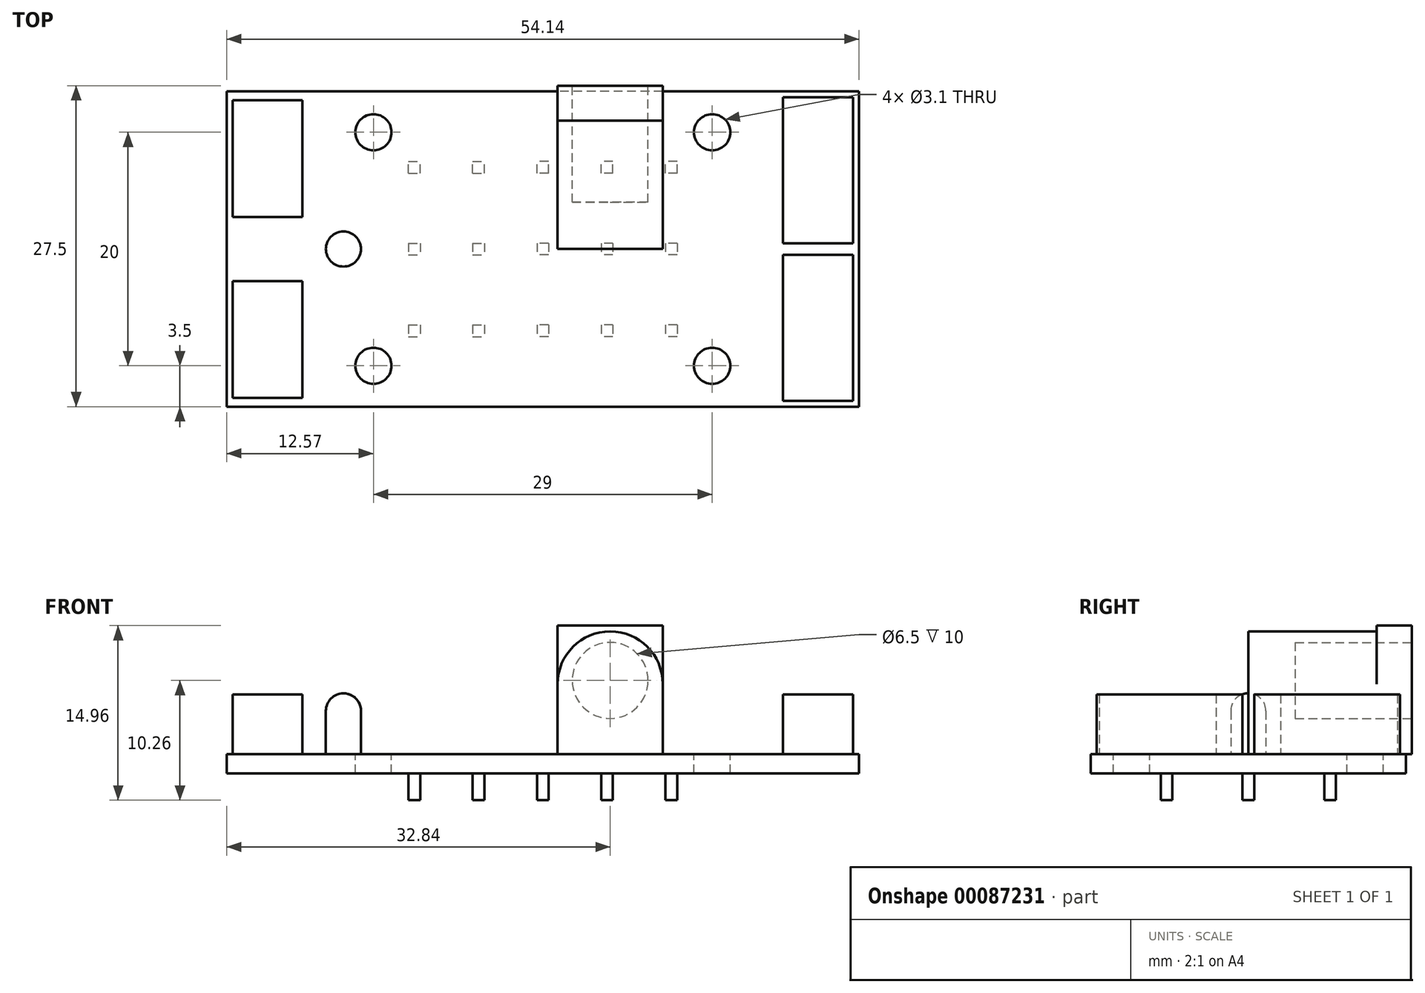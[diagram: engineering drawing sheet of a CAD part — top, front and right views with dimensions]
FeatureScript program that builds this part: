
annotation { "Feature Type Name" : "Feature", "Feature Type Description" : "" }
export const myFeature = defineFeature(function(context is Context, id is Id, definition is map)
    precondition{}
    {
        {
            var Q0;
            Q0=qCreatedBy(makeId("Top.planeOp"),FACE);
            var sketch = newSketch(context, id + "F0", { "sketchPlane" : qUnion([Q0])});
            skLineSegment(sketch, "E0.bottom", {"start": v(27.07, -13.5) * mm, "end": v(-27.07, -13.5) * mm});
            skLineSegment(sketch, "E0.top", {"start": v(27.07, 13.5) * mm, "end": v(-27.07, 13.5) * mm});
            skLineSegment(sketch, "E0.left", {"start": v(27.07, -13.5) * mm, "end": v(27.07, 13.5) * mm});
            skLineSegment(sketch, "E0.right", {"start": v(-27.07, -13.5) * mm, "end": v(-27.07, 13.5) * mm});
            skPoint(sketch, "E0.middle", {"position": v(0, 0) * mm});
            skCircle(sketch, "E1", {"center": v(-14.5, 10) * mm, "radius": 1.55 * mm});
            skCircle(sketch, "E2.MirrorC", {"center": v(14.5, 10) * mm, "radius": 1.55 * mm});
            skCircle(sketch, "E3.MirrorC", {"center": v(14.5, -10) * mm, "radius": 1.55 * mm});
            skCircle(sketch, "E4.MirrorC", {"center": v(-14.5, -10) * mm, "radius": 1.55 * mm});
            skLineSegment(sketch, "E5.bottom", {"start": v(26.57, 0.5) * mm, "end": v(20.57, 0.5) * mm});
            skLineSegment(sketch, "E5.top", {"start": v(26.57, 13) * mm, "end": v(20.57, 13) * mm});
            skLineSegment(sketch, "E5.left", {"start": v(26.57, 0.5) * mm, "end": v(26.57, 13) * mm});
            skLineSegment(sketch, "E5.right", {"start": v(20.57, 0.5) * mm, "end": v(20.57, 13) * mm});
            skPoint(sketch, "E5.middle", {"position": v(23.57, 6.75) * mm});
            skLineSegment(sketch, "E6.MirrorCS", {"start": v(26.57, -0.5) * mm, "end": v(20.57, -0.5) * mm});
            skLineSegment(sketch, "E7.MirrorCS", {"start": v(26.57, -0.5) * mm, "end": v(26.57, -13) * mm});
            skLineSegment(sketch, "E8.MirrorCS", {"start": v(20.57, -0.5) * mm, "end": v(20.57, -13) * mm});
            skLineSegment(sketch, "E9.MirrorCS", {"start": v(26.57, -13) * mm, "end": v(20.57, -13) * mm});
            skLineSegment(sketch, "E10.bottom", {"start": v(10.27, 0) * mm, "end": v(1.27, 0) * mm});
            skLineSegment(sketch, "E10.top", {"start": v(10.27, 14) * mm, "end": v(1.27, 14) * mm});
            skLineSegment(sketch, "E10.left", {"start": v(10.27, 0) * mm, "end": v(10.27, 14) * mm});
            skLineSegment(sketch, "E10.right", {"start": v(1.27, 0) * mm, "end": v(1.27, 14) * mm});
            skPoint(sketch, "E10.middle", {"position": v(5.77, 7) * mm});
            skLineSegment(sketch, "E11.bottom", {"start": v(-11.07, -11) * mm, "end": v(-1.07, -11) * mm});
            skLineSegment(sketch, "E11.top", {"start": v(-11.07, 11) * mm, "end": v(-1.07, 11) * mm});
            skLineSegment(sketch, "E11.left", {"start": v(-11.07, -11) * mm, "end": v(-11.07, 11) * mm});
            skLineSegment(sketch, "E11.right", {"start": v(-1.07, -11) * mm, "end": v(-1.07, 11) * mm});
            skPoint(sketch, "E11.middle", {"position": v(-6.07, 0) * mm});
            skCircle(sketch, "E12", {"center": v(-17.07, 0) * mm, "radius": 1.5 * mm});
            skLineSegment(sketch, "E13.bottom", {"start": v(-20.57, 2.75) * mm, "end": v(-26.57, 2.75) * mm});
            skLineSegment(sketch, "E13.top", {"start": v(-20.57, 12.75) * mm, "end": v(-26.57, 12.75) * mm});
            skLineSegment(sketch, "E13.left", {"start": v(-20.57, 2.75) * mm, "end": v(-20.57, 12.75) * mm});
            skLineSegment(sketch, "E13.right", {"start": v(-26.57, 2.75) * mm, "end": v(-26.57, 12.75) * mm});
            skPoint(sketch, "E13.middle", {"position": v(-23.57, 7.75) * mm});
            skLineSegment(sketch, "E14.MirrorCS", {"start": v(-20.57, -2.75) * mm, "end": v(-26.57, -2.75) * mm});
            skLineSegment(sketch, "E15.MirrorCS", {"start": v(-26.57, -2.75) * mm, "end": v(-26.57, -12.75) * mm});
            skLineSegment(sketch, "E16.MirrorCS", {"start": v(-20.57, -2.75) * mm, "end": v(-20.57, -12.75) * mm});
            skLineSegment(sketch, "E17.MirrorCS", {"start": v(-20.57, -12.75) * mm, "end": v(-26.57, -12.75) * mm});
            skLineSegment(sketch, "E18", {"start": v(1.27, 11) * mm, "end": v(10.27, 11) * mm});
            skSolve(sketch);
        }
        {
            var Q0;
            Q0=makeQuery(id+"F0.imprint","IMPRINT",FACE,{"disambiguationData":[TD([[makeQuery(id+"F0.imprint","IMPRINT",EDGE,{"derivedFrom":sQuery(id+"F0.wireOp",EDGE,"E13.bottom")}),-1.0]])]});
            var Q1;
            Q1=makeQuery(id+"F0.imprint","IMPRINT",FACE,{"disambiguationData":[TD([[makeQuery(id+"F0.imprint","IMPRINT",EDGE,{"derivedFrom":sQuery(id+"F0.wireOp",EDGE,"E0.bottom")}),-1.0]])]});
            var Q2;
            Q2=makeQuery(id+"F0.imprint","IMPRINT",FACE,{"disambiguationData":[TD([[makeQuery(id+"F0.imprint","IMPRINT",EDGE,{"derivedFrom":sQuery(id+"F0.wireOp",EDGE,"E14.MirrorCS")}),1.0]])]});
            var Q3;
            Q3=makeQuery(id+"F0.imprint","IMPRINT",FACE,{"disambiguationData":[TD([[makeQuery(id+"F0.imprint","IMPRINT",EDGE,{"derivedFrom":sQuery(id+"F0.wireOp",EDGE,"E11.bottom")}),1.0]])]});
            var Q4;
            {var subQ5=sQuery(id+"F0.wireOp",EDGE,"E10.bottom");Q4=makeQuery(id+"F0.imprint","IMPRINT",FACE,{"disambiguationData":[TD([[makeQuery(id+"F0.imprint","IMPRINT",EDGE,{"derivedFrom":subQ5}),-1.0]])]});}
            var Q5;
            Q5=makeQuery(id+"F0.imprint","IMPRINT",FACE,{"disambiguationData":[TD([[makeQuery(id+"F0.imprint","IMPRINT",EDGE,{"derivedFrom":sQuery(id+"F0.wireOp",EDGE,"E5.bottom")}),-1.0]])]});
            var Q6;
            Q6=makeQuery(id+"F0.imprint","IMPRINT",FACE,{"disambiguationData":[TD([[makeQuery(id+"F0.imprint","IMPRINT",EDGE,{"derivedFrom":sQuery(id+"F0.wireOp",EDGE,"E6.MirrorCS")}),1.0]])]});
            var Q7;
            Q7=makeQuery(id+"F0.imprint","IMPRINT",FACE,{"disambiguationData":[TD([[makeQuery(id+"F0.imprint","IMPRINT",EDGE,{"derivedFrom":sQuery(id+"F0.wireOp",EDGE,"E12")}),1.0]])]});
            var Q8;
            {var subQ5=sQuery(id+"F0.wireOp",EDGE,"E18");Q8=makeQuery(id+"F0.imprint","IMPRINT",FACE,{"disambiguationData":[TD([[makeQuery(id+"F0.imprint","IMPRINT",EDGE,{"derivedFrom":subQ5}),1.0]])]});}
            extrude(context, id + "F1", {"entities" : qUnion([Q0, Q1, Q2, Q3, Q4, Q5, Q6, Q7, Q8]), "oppositeDirection" : true, "depth" : 1.66 * mm});
        }
        {
            var Q0;
            {var subQ5=sQuery(id+"F0.wireOp",EDGE,"E18");Q0=makeQuery(id+"F0.imprint","IMPRINT",FACE,{"disambiguationData":[TD([[makeQuery(id+"F0.imprint","IMPRINT",EDGE,{"derivedFrom":subQ5}),1.0]])]});}
            var Q1;
            {var subQ5=sQuery(id+"F0.wireOp",EDGE,"E10.top");Q1=makeQuery(id+"F0.imprint","IMPRINT",FACE,{"disambiguationData":[TD([[makeQuery(id+"F0.imprint","IMPRINT",EDGE,{"derivedFrom":subQ5}),1.0]])]});}
            extrude(context, id + "F2", {"entities" : qUnion([Q0, Q1]), "depth" : 11 * mm});
        }
        {
            var Q0;
            {var subQ0=sQuery(id+"F0.wireOp",EDGE,"E10.bottom");Q0=makeQuery(id+"F0.imprint","IMPRINT",FACE,{"disambiguationData":[TD([[makeQuery(id+"F0.imprint","IMPRINT",EDGE,{"derivedFrom":subQ0}),-1.0]])]});}
            extrude(context, id + "F3", {"entities" : qUnion([Q0]), "operationType" : NewBodyOperationType.ADD, "depth" : 10.5 * mm});
        }
        {
            var Q0;
            Q0=makeQuery(id+"F3.opExtrude","CAP_EDGE",EDGE,{"disambiguationData":[OSD([sQuery(id+"F0.wireOp",EDGE,"E10.right")])],"isStart":false});
            var Q1;
            Q1=makeQuery(id+"F3.opExtrude","CAP_EDGE",EDGE,{"disambiguationData":[OSD([sQuery(id+"F0.wireOp",EDGE,"E10.left")])],"isStart":false});
            fillet(context, id + "F4", {"entities" : qUnion([Q0, Q1]), "radius" : 4.5 * mm, "tangentPropagation" : true, "allowEdgeOverflow" : false});
        }
        {
            var Q0;
            Q0=makeQuery(id+"F2.opExtrude","SWEPT_FACE",FACE,{"disambiguationData":[OSD([sQuery(id+"F0.wireOp",EDGE,"E10.top")])]});
            var sketch = newSketch(context, id + "F5", { "sketchPlane" : qUnion([Q0])});
            skCircle(sketch, "E19", {"center": v(-5.77, 6.3) * mm, "radius": 3.25 * mm});
            skPoint(sketch, "E19.centerSnap0", {"position": v(-5.77, 0) * mm});
            skSolve(sketch);
        }
        {
            var Q0;
            Q0=makeQuery(id+"F5.imprint","IMPRINT",FACE,{"disambiguationData":[TD([[makeQuery(id+"F5.imprint","IMPRINT",EDGE,{"derivedFrom":sQuery(id+"F5.wireOp",EDGE,"E19")}),1.0]])]});
            extrude(context, id + "F6", {"entities" : qUnion([Q0]), "operationType" : NewBodyOperationType.REMOVE, "oppositeDirection" : true, "depth" : 10 * mm});
        }
        {
            var Q0;
            Q0=makeQuery(id+"F0.imprint","IMPRINT",FACE,{"disambiguationData":[TD([[makeQuery(id+"F0.imprint","IMPRINT",EDGE,{"derivedFrom":sQuery(id+"F0.wireOp",EDGE,"E12")}),1.0]])]});
            extrude(context, id + "F7", {"entities" : qUnion([Q0]), "depth" : 5.2 * mm});
        }
        {
            var Q0;
            Q0=makeQuery(id+"F7.opExtrude","CAP_EDGE",EDGE,{"disambiguationData":[OSD([sQuery(id+"F0.wireOp",EDGE,"E12")])],"isStart":false});
            fillet(context, id + "F8", {"entities" : qUnion([Q0]), "radius" : 1.5 * mm, "tangentPropagation" : true, "allowEdgeOverflow" : false});
        }
        {
            var Q0;
            Q0=makeQuery(id+"F0.imprint","IMPRINT",FACE,{"disambiguationData":[TD([[makeQuery(id+"F0.imprint","IMPRINT",EDGE,{"derivedFrom":sQuery(id+"F0.wireOp",EDGE,"E5.bottom")}),-1.0]])]});
            var Q1;
            Q1=makeQuery(id+"F0.imprint","IMPRINT",FACE,{"disambiguationData":[TD([[makeQuery(id+"F0.imprint","IMPRINT",EDGE,{"derivedFrom":sQuery(id+"F0.wireOp",EDGE,"E6.MirrorCS")}),1.0]])]});
            var Q2;
            Q2=makeQuery(id+"F0.imprint","IMPRINT",FACE,{"disambiguationData":[TD([[makeQuery(id+"F0.imprint","IMPRINT",EDGE,{"derivedFrom":sQuery(id+"F0.wireOp",EDGE,"E14.MirrorCS")}),1.0]])]});
            var Q3;
            Q3=makeQuery(id+"F0.imprint","IMPRINT",FACE,{"disambiguationData":[TD([[makeQuery(id+"F0.imprint","IMPRINT",EDGE,{"derivedFrom":sQuery(id+"F0.wireOp",EDGE,"E13.bottom")}),-1.0]])]});
            extrude(context, id + "F9", {"entities" : qUnion([Q0, Q1, Q2, Q3]), "depth" : 5.1 * mm});
        }
        {
            var Q0;
            Q0=makeQuery(id+"F1.opExtrude","CAP_FACE",FACE,{"disambiguationData":[OSD([sQuery(id+"F0.wireOp",EDGE,"E0.bottom"),sQuery(id+"F0.wireOp",EDGE,"E0.top"),sQuery(id+"F0.wireOp",EDGE,"E0.left"),sQuery(id+"F0.wireOp",EDGE,"E0.right"),sQuery(id+"F0.wireOp",EDGE,"E1"),sQuery(id+"F0.wireOp",EDGE,"E2.MirrorC"),sQuery(id+"F0.wireOp",EDGE,"E3.MirrorC"),sQuery(id+"F0.wireOp",EDGE,"E4.MirrorC")])],"isStart":false});
            var sketch = newSketch(context, id + "F10", { "sketchPlane" : qUnion([Q0])});
            skLineSegment(sketch, "E20.bottom", {"start": v(0.5, -0.5) * mm, "end": v(-0.5, -0.5) * mm});
            skLineSegment(sketch, "E20.top", {"start": v(0.5, 0.5) * mm, "end": v(-0.5, 0.5) * mm});
            skLineSegment(sketch, "E20.left", {"start": v(0.5, -0.5) * mm, "end": v(0.5, 0.5) * mm});
            skLineSegment(sketch, "E20.right", {"start": v(-0.5, -0.5) * mm, "end": v(-0.5, 0.5) * mm});
            skPoint(sketch, "E20.middle", {"position": v(0, 0) * mm});
            skLineSegment(sketch, "E21.0.1.0", {"start": v(0.5, 6.5) * mm, "end": v(0.5, 7.5) * mm});
            skLineSegment(sketch, "E21.0.1.1", {"start": v(0.5, 7.5) * mm, "end": v(-0.5, 7.5) * mm});
            skLineSegment(sketch, "E21.0.1.2", {"start": v(-0.5, 6.5) * mm, "end": v(-0.5, 7.5) * mm});
            skLineSegment(sketch, "E21.0.1.3", {"start": v(0.5, 6.5) * mm, "end": v(-0.5, 6.5) * mm});
            skLineSegment(sketch, "E21.1.0.0", {"start": v(6, -0.5) * mm, "end": v(6, 0.5) * mm});
            skLineSegment(sketch, "E21.1.0.1", {"start": v(6, 0.5) * mm, "end": v(5, 0.5) * mm});
            skLineSegment(sketch, "E21.1.0.2", {"start": v(5, -0.5) * mm, "end": v(5, 0.5) * mm});
            skLineSegment(sketch, "E21.1.0.3", {"start": v(6, -0.5) * mm, "end": v(5, -0.5) * mm});
            skLineSegment(sketch, "E21.1.1.0", {"start": v(6, 6.5) * mm, "end": v(6, 7.5) * mm});
            skLineSegment(sketch, "E21.1.1.1", {"start": v(6, 7.5) * mm, "end": v(5, 7.5) * mm});
            skLineSegment(sketch, "E21.1.1.2", {"start": v(5, 6.5) * mm, "end": v(5, 7.5) * mm});
            skLineSegment(sketch, "E21.1.1.3", {"start": v(6, 6.5) * mm, "end": v(5, 6.5) * mm});
            skLineSegment(sketch, "E21.2.0.0", {"start": v(11.5, -0.5) * mm, "end": v(11.5, 0.5) * mm});
            skLineSegment(sketch, "E21.2.0.1", {"start": v(11.5, 0.5) * mm, "end": v(10.5, 0.5) * mm});
            skLineSegment(sketch, "E21.2.0.2", {"start": v(10.5, -0.5) * mm, "end": v(10.5, 0.5) * mm});
            skLineSegment(sketch, "E21.2.0.3", {"start": v(11.5, -0.5) * mm, "end": v(10.5, -0.5) * mm});
            skLineSegment(sketch, "E21.2.1.0", {"start": v(11.5, 6.5) * mm, "end": v(11.5, 7.5) * mm});
            skLineSegment(sketch, "E21.2.1.1", {"start": v(11.5, 7.5) * mm, "end": v(10.5, 7.5) * mm});
            skLineSegment(sketch, "E21.2.1.2", {"start": v(10.5, 6.5) * mm, "end": v(10.5, 7.5) * mm});
            skLineSegment(sketch, "E21.2.1.3", {"start": v(11.5, 6.5) * mm, "end": v(10.5, 6.5) * mm});
            skLineSegment(sketch, "E21.direction1", {"start": v(0.5, -0.5) * mm, "end": v(6, -0.5) * mm, "construction": true});
            skLineSegment(sketch, "E21.direction2", {"start": v(0.5, -0.5) * mm, "end": v(0.5, 6.5) * mm, "construction": true});
            skLineSegment(sketch, "E22.MirrorCS", {"start": v(11.5, -6.5) * mm, "end": v(10.5, -6.5) * mm});
            skLineSegment(sketch, "E23.MirrorCS", {"start": v(11.5, -6.5) * mm, "end": v(11.5, -7.5) * mm});
            skLineSegment(sketch, "E24.MirrorCS", {"start": v(11.5, -7.5) * mm, "end": v(10.5, -7.5) * mm});
            skLineSegment(sketch, "E25.MirrorCS", {"start": v(10.5, -6.5) * mm, "end": v(10.5, -7.5) * mm});
            skLineSegment(sketch, "E26.MirrorCS", {"start": v(6, -6.5) * mm, "end": v(5, -6.5) * mm});
            skLineSegment(sketch, "E27.MirrorCS", {"start": v(6, -6.5) * mm, "end": v(6, -7.5) * mm});
            skLineSegment(sketch, "E28.MirrorCS", {"start": v(6, -7.5) * mm, "end": v(5, -7.5) * mm});
            skLineSegment(sketch, "E29.MirrorCS", {"start": v(5, -6.5) * mm, "end": v(5, -7.5) * mm});
            skLineSegment(sketch, "E30.MirrorCS", {"start": v(0.5, -6.5) * mm, "end": v(-0.5, -6.5) * mm});
            skLineSegment(sketch, "E31.MirrorCS", {"start": v(-0.5, -6.5) * mm, "end": v(-0.5, -7.5) * mm});
            skLineSegment(sketch, "E32.MirrorCS", {"start": v(0.5, -6.5) * mm, "end": v(0.5, -7.5) * mm});
            skLineSegment(sketch, "E33.MirrorCS", {"start": v(0.5, -7.5) * mm, "end": v(-0.5, -7.5) * mm});
            skLineSegment(sketch, "E34.MirrorCS", {"start": v(-6, -6.5) * mm, "end": v(-6, -7.5) * mm});
            skLineSegment(sketch, "E35.MirrorCS", {"start": v(-10.5, 6.5) * mm, "end": v(-10.5, 7.5) * mm});
            skLineSegment(sketch, "E36.MirrorCS", {"start": v(-11.5, -0.5) * mm, "end": v(-10.5, -0.5) * mm});
            skLineSegment(sketch, "E37.MirrorCS", {"start": v(-11.5, -6.5) * mm, "end": v(-10.5, -6.5) * mm});
            skLineSegment(sketch, "E38.MirrorCS", {"start": v(-10.5, -0.5) * mm, "end": v(-10.5, 0.5) * mm});
            skLineSegment(sketch, "E39.MirrorCS", {"start": v(-0.5, -0.5) * mm, "end": v(-6, -0.5) * mm, "construction": true});
            skLineSegment(sketch, "E40.MirrorCS", {"start": v(-11.5, 7.5) * mm, "end": v(-10.5, 7.5) * mm});
            skLineSegment(sketch, "E41.MirrorCS", {"start": v(-6, -6.5) * mm, "end": v(-5, -6.5) * mm});
            skLineSegment(sketch, "E42.MirrorCS", {"start": v(-11.5, -6.5) * mm, "end": v(-11.5, -7.5) * mm});
            skLineSegment(sketch, "E43.MirrorCS", {"start": v(-11.5, -0.5) * mm, "end": v(-11.5, 0.5) * mm});
            skLineSegment(sketch, "E44.MirrorCS", {"start": v(-6, -7.5) * mm, "end": v(-5, -7.5) * mm});
            skLineSegment(sketch, "E45.MirrorCS", {"start": v(-5, 6.5) * mm, "end": v(-5, 7.5) * mm});
            skLineSegment(sketch, "E46.MirrorCS", {"start": v(-6, 6.5) * mm, "end": v(-5, 6.5) * mm});
            skLineSegment(sketch, "E47.MirrorCS", {"start": v(-11.5, -7.5) * mm, "end": v(-10.5, -7.5) * mm});
            skLineSegment(sketch, "E48.MirrorCS", {"start": v(-11.5, 0.5) * mm, "end": v(-10.5, 0.5) * mm});
            skLineSegment(sketch, "E49.MirrorCS", {"start": v(-5, -6.5) * mm, "end": v(-5, -7.5) * mm});
            skLineSegment(sketch, "E50.MirrorCS", {"start": v(-11.5, 6.5) * mm, "end": v(-10.5, 6.5) * mm});
            skLineSegment(sketch, "E51.MirrorCS", {"start": v(-6, 7.5) * mm, "end": v(-5, 7.5) * mm});
            skLineSegment(sketch, "E52.MirrorCS", {"start": v(-6, 6.5) * mm, "end": v(-6, 7.5) * mm});
            skLineSegment(sketch, "E53.MirrorCS", {"start": v(-6, -0.5) * mm, "end": v(-5, -0.5) * mm});
            skLineSegment(sketch, "E54.MirrorCS", {"start": v(-5, -0.5) * mm, "end": v(-5, 0.5) * mm});
            skLineSegment(sketch, "E55.MirrorCS", {"start": v(-11.5, 6.5) * mm, "end": v(-11.5, 7.5) * mm});
            skLineSegment(sketch, "E56.MirrorCS", {"start": v(-6, 0.5) * mm, "end": v(-5, 0.5) * mm});
            skLineSegment(sketch, "E57.MirrorCS", {"start": v(-10.5, -6.5) * mm, "end": v(-10.5, -7.5) * mm});
            skLineSegment(sketch, "E58.MirrorCS", {"start": v(-6, -0.5) * mm, "end": v(-6, 0.5) * mm});
            skSolve(sketch);
        }
        {
            var Q0;
            Q0=makeQuery(id+"F10.imprint","IMPRINT",FACE,{"disambiguationData":[TD([[makeQuery(id+"F10.imprint","IMPRINT",EDGE,{"derivedFrom":sQuery(id+"F10.wireOp",EDGE,"E20.bottom")}),-1.0]])]});
            var Q1;
            Q1=makeQuery(id+"F10.imprint","IMPRINT",FACE,{"disambiguationData":[TD([[makeQuery(id+"F10.imprint","IMPRINT",EDGE,{"derivedFrom":sQuery(id+"F10.wireOp",EDGE,"E21.0.1.0")}),1.0]])]});
            var Q2;
            Q2=makeQuery(id+"F10.imprint","IMPRINT",FACE,{"disambiguationData":[TD([[makeQuery(id+"F10.imprint","IMPRINT",EDGE,{"derivedFrom":sQuery(id+"F10.wireOp",EDGE,"E21.1.1.0")}),1.0]])]});
            var Q3;
            Q3=makeQuery(id+"F10.imprint","IMPRINT",FACE,{"disambiguationData":[TD([[makeQuery(id+"F10.imprint","IMPRINT",EDGE,{"derivedFrom":sQuery(id+"F10.wireOp",EDGE,"E21.2.1.0")}),1.0]])]});
            var Q4;
            Q4=makeQuery(id+"F10.imprint","IMPRINT",FACE,{"disambiguationData":[TD([[makeQuery(id+"F10.imprint","IMPRINT",EDGE,{"derivedFrom":sQuery(id+"F10.wireOp",EDGE,"E21.2.0.0")}),1.0]])]});
            var Q5;
            Q5=makeQuery(id+"F10.imprint","IMPRINT",FACE,{"disambiguationData":[TD([[makeQuery(id+"F10.imprint","IMPRINT",EDGE,{"derivedFrom":sQuery(id+"F10.wireOp",EDGE,"E21.1.0.0")}),1.0]])]});
            var Q6;
            Q6=makeQuery(id+"F10.imprint","IMPRINT",FACE,{"disambiguationData":[TD([[makeQuery(id+"F10.imprint","IMPRINT",EDGE,{"derivedFrom":sQuery(id+"F10.wireOp",EDGE,"E22.MirrorCS")}),1.0]])]});
            var Q7;
            Q7=makeQuery(id+"F10.imprint","IMPRINT",FACE,{"disambiguationData":[TD([[makeQuery(id+"F10.imprint","IMPRINT",EDGE,{"derivedFrom":sQuery(id+"F10.wireOp",EDGE,"E26.MirrorCS")}),1.0]])]});
            var Q8;
            Q8=makeQuery(id+"F10.imprint","IMPRINT",FACE,{"disambiguationData":[TD([[makeQuery(id+"F10.imprint","IMPRINT",EDGE,{"derivedFrom":sQuery(id+"F10.wireOp",EDGE,"E30.MirrorCS")}),1.0]])]});
            var Q9;
            Q9=makeQuery(id+"F10.imprint","IMPRINT",FACE,{"disambiguationData":[TD([[makeQuery(id+"F10.imprint","IMPRINT",EDGE,{"derivedFrom":sQuery(id+"F10.wireOp",EDGE,"E34.MirrorCS")}),1.0]])]});
            var Q10;
            Q10=makeQuery(id+"F10.imprint","IMPRINT",FACE,{"disambiguationData":[TD([[makeQuery(id+"F10.imprint","IMPRINT",EDGE,{"derivedFrom":sQuery(id+"F10.wireOp",EDGE,"E53.MirrorCS")}),1.0]])]});
            var Q11;
            Q11=makeQuery(id+"F10.imprint","IMPRINT",FACE,{"disambiguationData":[TD([[makeQuery(id+"F10.imprint","IMPRINT",EDGE,{"derivedFrom":sQuery(id+"F10.wireOp",EDGE,"E46.MirrorCS")}),1.0]])]});
            var Q12;
            Q12=makeQuery(id+"F10.imprint","IMPRINT",FACE,{"disambiguationData":[TD([[makeQuery(id+"F10.imprint","IMPRINT",EDGE,{"derivedFrom":sQuery(id+"F10.wireOp",EDGE,"E35.MirrorCS")}),1.0]])]});
            var Q13;
            Q13=makeQuery(id+"F10.imprint","IMPRINT",FACE,{"disambiguationData":[TD([[makeQuery(id+"F10.imprint","IMPRINT",EDGE,{"derivedFrom":sQuery(id+"F10.wireOp",EDGE,"E36.MirrorCS")}),1.0]])]});
            var Q14;
            Q14=makeQuery(id+"F10.imprint","IMPRINT",FACE,{"disambiguationData":[TD([[makeQuery(id+"F10.imprint","IMPRINT",EDGE,{"derivedFrom":sQuery(id+"F10.wireOp",EDGE,"E37.MirrorCS")}),-1.0]])]});
            extrude(context, id + "F11", {"entities" : qUnion([Q0, Q1, Q2, Q3, Q4, Q5, Q6, Q7, Q8, Q9, Q10, Q11, Q12, Q13, Q14]), "operationType" : NewBodyOperationType.ADD, "depth" : 2.3 * mm});
        }
    });
